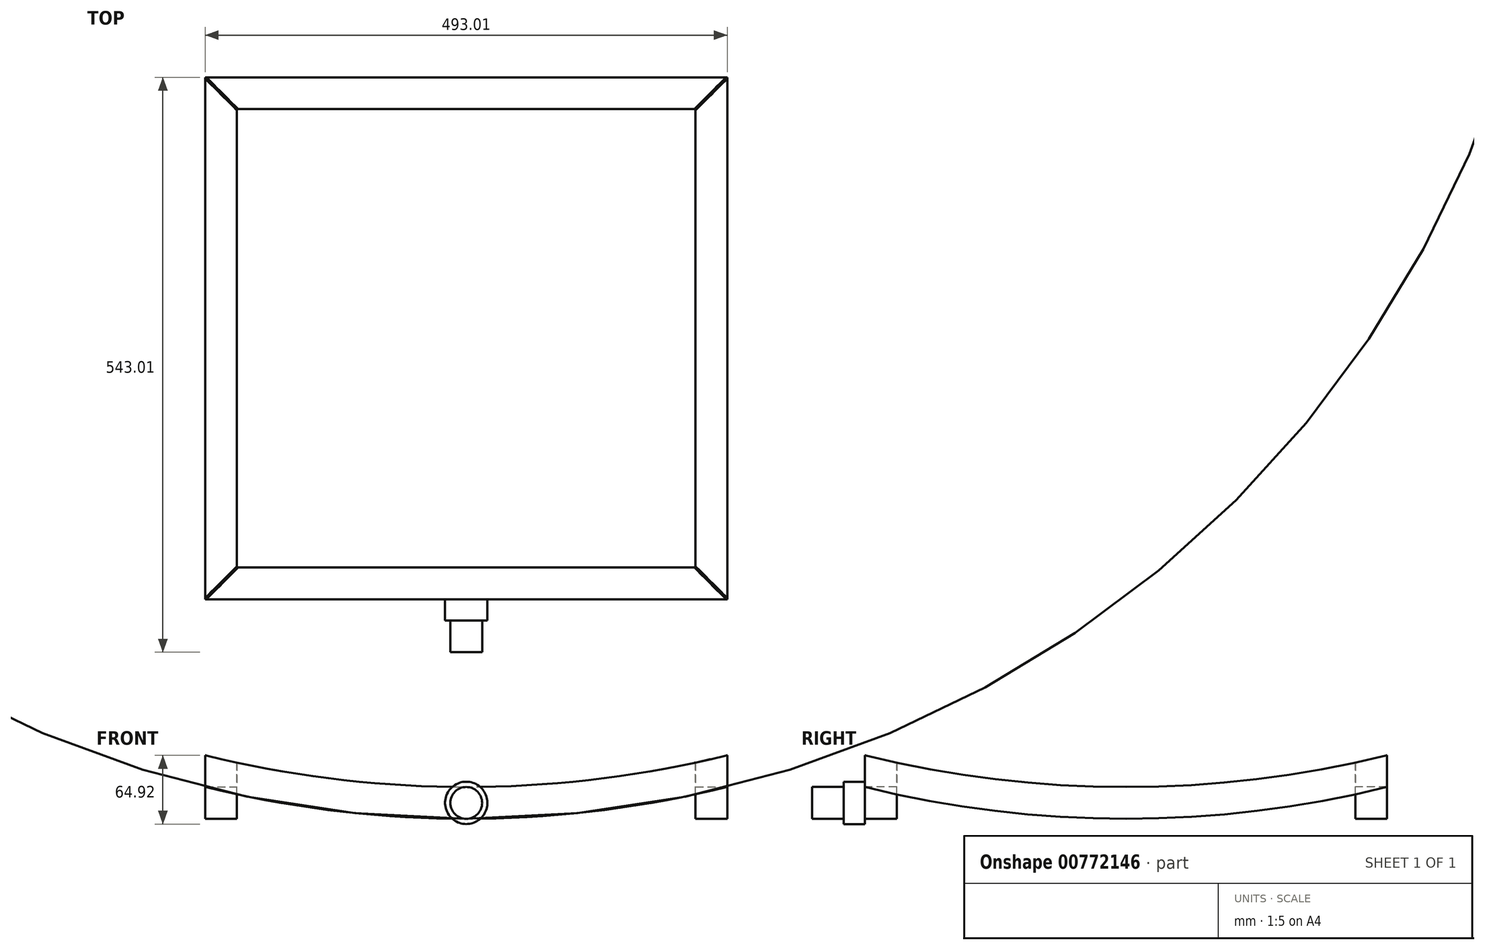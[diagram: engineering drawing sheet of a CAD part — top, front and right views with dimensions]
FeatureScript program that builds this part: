
annotation { "Feature Type Name" : "Feature", "Feature Type Description" : "" }
export const myFeature = defineFeature(function(context is Context, id is Id, definition is map)
    precondition{}
    {
        {
            var Q0;
            Q0=qCreatedBy(makeId("Top.planeOp"),FACE);
            var sketch = newSketch(context, id + "F0", { "sketchPlane" : qUnion([Q0])});
            skLineSegment(sketch, "E0.bottom", {"start": v(-170.08, -185.68) * mm, "end": v(322.93, -185.68) * mm});
            skLineSegment(sketch, "E0.top", {"start": v(-170.08, 307.33) * mm, "end": v(322.93, 307.33) * mm});
            skLineSegment(sketch, "E0.left", {"start": v(-170.08, -185.68) * mm, "end": v(-170.08, 307.33) * mm});
            skLineSegment(sketch, "E0.right", {"start": v(322.93, -185.68) * mm, "end": v(322.93, 307.33) * mm});
            skSolve(sketch);
        }
        {
            var Q0;
            Q0=makeQuery(id+"F0.imprint","IMPRINT",FACE,{"disambiguationData":[TD([[makeQuery(id+"F0.imprint","IMPRINT",EDGE,{"derivedFrom":sQuery(id+"F0.wireOp",EDGE,"E0.bottom")}),1.0]])]});
            extrude(context, id + "F1", {"entities" : qUnion([Q0]), "depth" : 60 * mm, "offsetDistance" : 25.4 * mm});
        }
        {
            var Q0;
            Q0=makeQuery(id+"F1.opExtrude","SWEPT_FACE",FACE,{"disambiguationData":[OSD([sQuery(id+"F0.wireOp",EDGE,"E0.bottom")])]});
            var sketch = newSketch(context, id + "F2", { "sketchPlane" : qUnion([Q0])});
            skLineSegment(sketch, "E1", {"start": v(-170.08, 60) * mm, "end": v(-200.08, 60) * mm});
            skLineSegment(sketch, "E2", {"start": v(-200.08, 60) * mm, "end": v(-200.08, 30) * mm});
            skLineSegment(sketch, "E3", {"start": v(-200.08, 30) * mm, "end": v(-170.08, 30) * mm});
            skLineSegment(sketch, "E4", {"start": v(-170.08, 30) * mm, "end": v(-170.08, 60) * mm});
            skLineSegment(sketch, "E5", {"start": v(322.93, 60) * mm, "end": v(352.93, 60) * mm});
            skLineSegment(sketch, "E6", {"start": v(352.93, 60) * mm, "end": v(352.93, 30) * mm});
            skLineSegment(sketch, "E7", {"start": v(352.93, 30) * mm, "end": v(322.93, 30) * mm});
            skLineSegment(sketch, "E8", {"start": v(322.93, 30) * mm, "end": v(322.93, 0) * mm});
            skLineSegment(sketch, "E9", {"start": v(76.43, 0) * mm, "end": v(76.43, 30) * mm});
            skArc(sketch, "E10", {"start": v(-170.08, 60) * mm, "mid": v(76.43, 30) * mm, "end": v(322.93, 60) * mm});
            skArc(sketch, "E11", {"start": v(-170.08, 30) * mm, "mid": v(76.43, 0) * mm, "end": v(322.93, 30) * mm});
            skLineSegment(sketch, "E12.bottom", {"start": v(-211.42, 82.44) * mm, "end": v(375.68, 82.44) * mm});
            skLineSegment(sketch, "E12.top", {"start": v(-211.42, -16.9) * mm, "end": v(375.68, -16.9) * mm});
            skLineSegment(sketch, "E12.left", {"start": v(-211.42, 82.44) * mm, "end": v(-211.42, -16.9) * mm});
            skLineSegment(sketch, "E12.right", {"start": v(375.68, 82.44) * mm, "end": v(375.68, -16.9) * mm});
            skSolve(sketch);
        }
        {
            var Q0;
            Q0=makeQuery(id+"F2.imprint","IMPRINT",FACE,{"disambiguationData":[TD([[makeQuery(id+"F2.imprint","IMPRINT",EDGE,{"derivedFrom":sQuery(id+"F2.wireOp",EDGE,"E1")}),-1.0]])]});
            var Q1;
            {var subQ1=sQuery(id+"F0.wireOp",EDGE,"E0.bottom");var subQ2=makeQuery(id+"F1.opExtrude","CAP_EDGE",EDGE,{"disambiguationData":[OSD([subQ1])],"isStart":false});Q1=makeQuery(id+"F2.imprint","IMPRINT",FACE,{"disambiguationData":[TD([[makeQuery(id+"F2.imprint","IMPRINT",EDGE,{"derivedFrom":subQ2}),-1.0]])]});}
            var Q2;
            {var subQ1=sQuery(id+"F0.wireOp",EDGE,"E0.bottom");var subQ2=makeQuery(id+"F1.opExtrude","SWEPT_EDGE",EDGE,{"disambiguationData":[OSD([subQ1,sQuery(id+"F0.wireOp",EDGE,"E0.left")])]});var subQ4=makeQuery(id+"F1.opExtrude","CAP_EDGE",EDGE,{"disambiguationData":[OSD([subQ1])],"isStart":true});var subQ6=makeQuery(id+"F2.imprint","INTERSECT",VERTEX,{"derivedFrom":[subQ2,subQ4]});Q2=makeQuery(id+"F2.imprint","IMPRINT",FACE,{"disambiguationData":[TD([[makeQuery(id+"F2.imprint","IMPRINT",EDGE,{"disambiguationData":[TD([[subQ6,-1.0]])],"derivedFrom":subQ4}),1.0]])]});}
            var Q3;
            {var subQ0=sQuery(id+"F2.wireOp",EDGE,"E8");Q3=makeQuery(id+"F2.imprint","IMPRINT",FACE,{"disambiguationData":[TD([[makeQuery(id+"F2.imprint","IMPRINT",EDGE,{"derivedFrom":subQ0}),-1.0]])]});}
            extrude(context, id + "F3", {"entities" : qUnion([Q0, Q1, Q2, Q3]), "operationType" : NewBodyOperationType.REMOVE, "oppositeDirection" : true, "depth" : 558.04 * mm, "offsetDistance" : 25.4 * mm});
        }
        {
            var Q0;
            Q0=makeQuery(id+"F1.opExtrude","SWEPT_FACE",FACE,{"disambiguationData":[OSD([sQuery(id+"F0.wireOp",EDGE,"E0.right")])]});
            var sketch = newSketch(context, id + "F4", { "sketchPlane" : qUnion([Q0])});
            skLineSegment(sketch, "E13", {"start": v(60.83, 30) * mm, "end": v(60.83, 0) * mm});
            skArc(sketch, "E14", {"start": v(-185.68, 60) * mm, "mid": v(60.83, 30) * mm, "end": v(307.33, 60) * mm});
            skSolve(sketch);
        }
        {
            var Q0;
            {var subQ1=sQuery(id+"F0.wireOp",EDGE,"E0.right");var subQ2=sQuery(id+"F0.wireOp",EDGE,"E0.bottom");var subQ3=makeQuery(id+"F3.boolean.opBoolean","MERGE",EDGE,{"derivedFrom":[makeQuery(id+"F1.opExtrude","CAP_EDGE",EDGE,{"disambiguationData":[OSD([subQ1])],"isStart":false}),makeQuery(id+"F3.opExtrude","SWEPT_EDGE",EDGE,{"disambiguationData":[OSD([subQ2,subQ1,sQuery(id+"F2.wireOp",EDGE,"E5"),sQuery(id+"F2.wireOp",EDGE,"E10")])]})]});Q0=makeQuery(id+"F4.imprint","IMPRINT",FACE,{"disambiguationData":[TD([[makeQuery(id+"F4.imprint","IMPRINT",EDGE,{"derivedFrom":subQ3}),-1.0]])]});}
            extrude(context, id + "F5", {"entities" : qUnion([Q0]), "operationType" : NewBodyOperationType.REMOVE, "oppositeDirection" : true, "depth" : 529.34 * mm, "offsetDistance" : 25.4 * mm});
        }
        {
            var Q0;
            {var subQ0=makeQuery(id+"F1.opExtrude","SWEPT_FACE",FACE,{"disambiguationData":[OSD([sQuery(id+"F0.wireOp",EDGE,"E0.right")])]});Q0=makeQuery(id+"F5.boolean.opBoolean","SPLIT",FACE,{"disambiguationData":[TD([makeQuery(id+"F1.opExtrude","SWEPT_FACE",FACE,{"disambiguationData":[OSD([sQuery(id+"F0.wireOp",EDGE,"E0.bottom")])]})])],"derivedFrom":subQ0});}
            var sketch = newSketch(context, id + "F6", { "sketchPlane" : qUnion([Q0])});
            skArc(sketch, "E15.0.0", {"start": v(60.83, 30) * mm, "mid": v(-63.34, 37.52) * mm, "end": v(-185.68, 60) * mm});
            skLineSegment(sketch, "E15.0.1", {"start": v(-185.68, 60) * mm, "end": v(-185.68, 30) * mm});
            skLineSegment(sketch, "E15.0.2", {"start": v(-185.68, 30) * mm, "end": v(60.83, 30) * mm});
            skArc(sketch, "E16.0.0", {"start": v(307.33, 60) * mm, "mid": v(185, 37.52) * mm, "end": v(60.83, 30) * mm});
            skLineSegment(sketch, "E16.0.1", {"start": v(60.83, 30) * mm, "end": v(307.33, 30) * mm});
            skLineSegment(sketch, "E16.0.2", {"start": v(307.33, 30) * mm, "end": v(307.33, 60) * mm});
            skLineSegment(sketch, "E17", {"start": v(60.83, 30) * mm, "end": v(60.83, 0) * mm});
            skArc(sketch, "E18", {"start": v(-185.68, 30) * mm, "mid": v(60.83, 0) * mm, "end": v(307.33, 30) * mm});
            skSolve(sketch);
        }
        {
            var Q0;
            {var subQ0=sQuery(id+"F6.wireOp",EDGE,"E15.0.2");Q0=makeQuery(id+"F6.imprint","IMPRINT",FACE,{"disambiguationData":[TD([[makeQuery(id+"F6.imprint","IMPRINT",EDGE,{"derivedFrom":subQ0}),1.0]])]});}
            var Q1;
            {var subQ0=sQuery(id+"F6.wireOp",EDGE,"E16.0.1");Q1=makeQuery(id+"F6.imprint","IMPRINT",FACE,{"disambiguationData":[TD([[makeQuery(id+"F6.imprint","IMPRINT",EDGE,{"derivedFrom":subQ0}),-1.0]])]});}
            extrude(context, id + "F7", {"entities" : qUnion([Q0, Q1]), "operationType" : NewBodyOperationType.ADD, "oppositeDirection" : true, "depth" : 493 * mm, "offsetDistance" : 25.4 * mm});
        }
        {
            var Q0;
            Q0=makeQuery(id+"F5.boolean.opBoolean","INTERSECT",EDGE,{"disambiguationData":[OD(1.0)],"derivedFrom":[makeQuery(id+"F3.boolean.opBoolean","COPY",FACE,{"derivedFrom":makeQuery(id+"F3.opExtrude","SWEPT_FACE",FACE,{"disambiguationData":[OSD([sQuery(id+"F2.wireOp",EDGE,"E10")])]})}),makeQuery(id+"F5.opExtrude","SWEPT_FACE",FACE,{"disambiguationData":[OSD([sQuery(id+"F4.wireOp",EDGE,"E14")])]})]});
            var Q1;
            Q1=makeQuery(id+"F5.boolean.opBoolean","INTERSECT",EDGE,{"disambiguationData":[OD(0.0)],"derivedFrom":[makeQuery(id+"F3.boolean.opBoolean","COPY",FACE,{"derivedFrom":makeQuery(id+"F3.opExtrude","SWEPT_FACE",FACE,{"disambiguationData":[OSD([sQuery(id+"F2.wireOp",EDGE,"E10")])]})}),makeQuery(id+"F5.opExtrude","SWEPT_FACE",FACE,{"disambiguationData":[OSD([sQuery(id+"F4.wireOp",EDGE,"E14")])]})]});
            fillet(context, id + "F8", {"entities" : qUnion([Q0, Q1]), "radius" : 5.08 * mm, "tangentPropagation" : true, "allowEdgeOverflow" : false});
        }
        {
            var Q0;
            Q0=qCreatedBy(makeId("Top.planeOp"),FACE);
            cPlane(context, id + "F9", {"entities" : qUnion([Q0]), "cplaneType" : CPlaneType.OFFSET, "offset" : 170.18 * mm, "width" : 152.4 * mm, "height" : 152.4 * mm});
        }
        {
            var Q0;
            Q0=qCreatedBy(id+"F9.planeOp",FACE);
            var sketch = newSketch(context, id + "F10", { "sketchPlane" : qUnion([Q0])});
            skLineSegment(sketch, "E19.0", {"start": v(321.72, 307.33) * mm, "end": v(-168.87, 307.33) * mm});
            skLineSegment(sketch, "E20.0", {"start": v(-170.08, 306.12) * mm, "end": v(-170.08, -184.47) * mm});
            skLineSegment(sketch, "E21.0", {"start": v(322.93, -184.47) * mm, "end": v(322.93, 306.12) * mm});
            skLineSegment(sketch, "E22.0", {"start": v(-168.87, -185.68) * mm, "end": v(321.72, -185.68) * mm});
            skPoint(sketch, "E23.0", {"position": v(-170.08, 307.33) * mm});
            skPoint(sketch, "E24.0", {"position": v(322.93, -185.68) * mm});
            skLineSegment(sketch, "E25", {"start": v(-170.08, 307.33) * mm, "end": v(-140.08, 307.33) * mm});
            skLineSegment(sketch, "E26", {"start": v(-140.08, 307.33) * mm, "end": v(-140.08, 277.33) * mm});
            skLineSegment(sketch, "E27", {"start": v(-140.08, 277.33) * mm, "end": v(-170.08, 277.33) * mm});
            skLineSegment(sketch, "E28", {"start": v(-170.08, 277.33) * mm, "end": v(-170.08, 307.33) * mm});
            skLineSegment(sketch, "E29", {"start": v(322.93, -185.68) * mm, "end": v(292.93, -185.68) * mm});
            skLineSegment(sketch, "E30", {"start": v(292.93, -185.68) * mm, "end": v(292.93, -155.68) * mm});
            skLineSegment(sketch, "E31", {"start": v(292.93, -155.68) * mm, "end": v(322.93, -155.68) * mm});
            skLineSegment(sketch, "E32", {"start": v(322.93, -155.68) * mm, "end": v(322.93, -185.68) * mm});
            skLineSegment(sketch, "E33.bottom", {"start": v(-140.08, 277.33) * mm, "end": v(292.93, 277.33) * mm});
            skLineSegment(sketch, "E33.top", {"start": v(-140.08, -155.68) * mm, "end": v(292.93, -155.68) * mm});
            skLineSegment(sketch, "E33.left", {"start": v(-140.08, 277.33) * mm, "end": v(-140.08, -155.68) * mm});
            skLineSegment(sketch, "E33.right", {"start": v(292.93, 277.33) * mm, "end": v(292.93, -155.68) * mm});
            skSolve(sketch);
        }
        {
            var Q0;
            Q0=makeQuery(id+"F10.imprint","IMPRINT",FACE,{"disambiguationData":[TD([[makeQuery(id+"F10.imprint","IMPRINT",EDGE,{"derivedFrom":sQuery(id+"F10.wireOp",EDGE,"E33.bottom")}),-1.0]])]});
            extrude(context, id + "F11", {"entities" : qUnion([Q0]), "operationType" : NewBodyOperationType.REMOVE, "oppositeDirection" : true, "depth" : 340.36 * mm, "offsetDistance" : 25.4 * mm});
        }
        {
            var Q0;
            Q0=makeQuery(id+"F1.opExtrude","SWEPT_FACE",FACE,{"disambiguationData":[OSD([sQuery(id+"F0.wireOp",EDGE,"E0.bottom")])]});
            var sketch = newSketch(context, id + "F12", { "sketchPlane" : qUnion([Q0])});
            skArc(sketch, "E34.0.0", {"start": v(321.72, 59.7) * mm, "mid": v(76.43, 30) * mm, "end": v(-168.87, 59.7) * mm});
            skFitSpline(sketch, "E34.0.1", {"points": [v(-168.87, 59.7) * mm, v(-169.27, 59.8) * mm, v(-169.67, 59.87) * mm, v(-170.08, 59.92) * mm]});
            skLineSegment(sketch, "E34.0.2", {"start": v(-170.08, 59.92) * mm, "end": v(-170.08, 30) * mm});
            skArc(sketch, "E34.0.3", {"start": v(-170.08, 30) * mm, "mid": v(76.43, 0) * mm, "end": v(322.93, 30) * mm});
            skLineSegment(sketch, "E34.0.4", {"start": v(322.93, 30) * mm, "end": v(322.93, 59.92) * mm});
            skFitSpline(sketch, "E34.0.5", {"points": [v(322.93, 59.92) * mm, v(322.52, 59.87) * mm, v(322.12, 59.8) * mm, v(321.72, 59.7) * mm]});
            skLineSegment(sketch, "E35", {"start": v(76.43, 30) * mm, "end": v(76.43, 0) * mm});
            skCircle(sketch, "E36", {"center": v(76.43, 15) * mm, "radius": 20 * mm});
            skSolve(sketch);
        }
        {
            var Q0;
            {var subQ0=sQuery(id+"F12.wireOp",EDGE,"E34.0.0");var subQ1=makeQuery(id+"F12.imprint","INTERSECT",VERTEX,{"derivedFrom":[subQ0,sQuery(id+"F12.wireOp",EDGE,"E35")]});Q0=makeQuery(id+"F12.imprint","IMPRINT",FACE,{"disambiguationData":[TD([[makeQuery(id+"F12.imprint","IMPRINT",EDGE,{"disambiguationData":[TD([[subQ1,1.0]])],"derivedFrom":subQ0}),1.0]])]});}
            var Q1;
            {var subQ0=sQuery(id+"F12.wireOp",EDGE,"E34.0.3");var subQ1=makeQuery(id+"F12.imprint","INTERSECT",VERTEX,{"derivedFrom":[subQ0,sQuery(id+"F12.wireOp",EDGE,"E35")]});Q1=makeQuery(id+"F12.imprint","IMPRINT",FACE,{"disambiguationData":[TD([[makeQuery(id+"F12.imprint","IMPRINT",EDGE,{"disambiguationData":[TD([[subQ1,1.0]])],"derivedFrom":subQ0}),-1.0]])]});}
            var Q2;
            {var subQ0=sQuery(id+"F12.wireOp",EDGE,"E35");Q2=makeQuery(id+"F12.imprint","IMPRINT",FACE,{"disambiguationData":[TD([[makeQuery(id+"F12.imprint","IMPRINT",EDGE,{"derivedFrom":subQ0}),1.0]])]});}
            var Q3;
            {var subQ0=sQuery(id+"F12.wireOp",EDGE,"E35");Q3=makeQuery(id+"F12.imprint","IMPRINT",FACE,{"disambiguationData":[TD([[makeQuery(id+"F12.imprint","IMPRINT",EDGE,{"derivedFrom":subQ0}),-1.0]])]});}
            extrude(context, id + "F13", {"entities" : qUnion([Q0, Q1, Q2, Q3]), "operationType" : NewBodyOperationType.ADD, "depth" : 20 * mm, "offsetDistance" : 25.4 * mm});
        }
        {
            var Q0;
            Q0=makeQuery(id+"F13.opExtrude","CAP_FACE",FACE,{"disambiguationData":[OSD([sQuery(id+"F12.wireOp",EDGE,"E36")])],"isStart":false});
            var sketch = newSketch(context, id + "F14", { "sketchPlane" : qUnion([Q0])});
            skCircle(sketch, "E37.0", {"center": v(76.43, 15) * mm, "radius": 20 * mm});
            skCircle(sketch, "E38", {"center": v(76.43, 15) * mm, "radius": 15 * mm});
            skSolve(sketch);
        }
        {
            var Q0;
            Q0=makeQuery(id+"F14.imprint","IMPRINT",FACE,{"disambiguationData":[TD([[makeQuery(id+"F14.imprint","IMPRINT",EDGE,{"derivedFrom":sQuery(id+"F14.wireOp",EDGE,"E38")}),1.0]])]});
            extrude(context, id + "F15", {"entities" : qUnion([Q0]), "operationType" : NewBodyOperationType.ADD, "depth" : 30 * mm, "offsetDistance" : 25.4 * mm});
        }
    });
